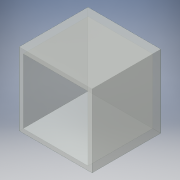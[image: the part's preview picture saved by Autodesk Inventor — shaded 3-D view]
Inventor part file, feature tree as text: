
AUTODESK INVENTOR PART (.ipt)
format: ipt  version: 2016 (Build 200138000, 138)  size: 103,936 bytes
history: native  units: mm
features: extrude x2, sketch x2
ambient origin geometry x8: Origin, YZ Plane, XZ Plane, XY Plane, X Axis, Y Axis, Z Axis, Center Point
bodies: Solid1 (feature_tree)
feature tree (4):
  extrude  "Extrusion1"  Depth=45.0mm
  extrude  "Extrusion2"  Depth=40.0mm
  sketch  "Sketch1"  dims[d0=45.0mm d1=45.0mm]
  sketch  "Sketch2"  dims[d2=40.0mm d3=40.0mm d4=40.0mm d5=0.0mm d6=2.5mm d7=0.0mm]
